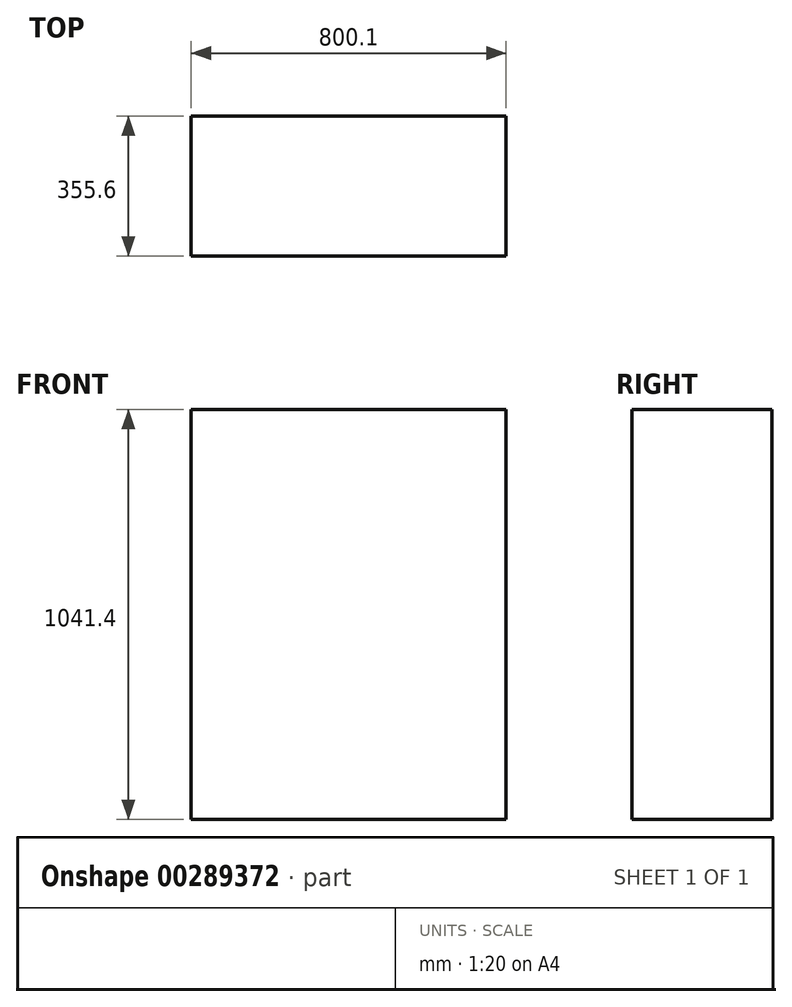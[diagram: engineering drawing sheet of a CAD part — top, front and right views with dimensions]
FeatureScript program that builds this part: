
annotation { "Feature Type Name" : "Feature", "Feature Type Description" : "" }
export const myFeature = defineFeature(function(context is Context, id is Id, definition is map)
    precondition{}
    {
        {
            var Q0;
            Q0=qCreatedBy(makeId("Front.planeOp"),FACE);
            var sketch = newSketch(context, id + "F0", { "sketchPlane" : qUnion([Q0])});
            skLineSegment(sketch, "E0.bottom", {"start": v(400.05, -520.7) * mm, "end": v(-400.05, -520.7) * mm});
            skLineSegment(sketch, "E0.top", {"start": v(400.05, 520.7) * mm, "end": v(-400.05, 520.7) * mm});
            skLineSegment(sketch, "E0.left", {"start": v(400.05, -520.7) * mm, "end": v(400.05, 520.7) * mm});
            skLineSegment(sketch, "E0.right", {"start": v(-400.05, -520.7) * mm, "end": v(-400.05, 520.7) * mm});
            skPoint(sketch, "E0.middle", {"position": v(0, 0) * mm});
            skSolve(sketch);
        }
        {
            var Q0;
            Q0=makeQuery(id+"F0.imprint","IMPRINT",FACE,{"disambiguationData":[TD([[makeQuery(id+"F0.imprint","IMPRINT",EDGE,{"derivedFrom":sQuery(id+"F0.wireOp",EDGE,"E0.bottom")}),-1.0]])]});
            extrude(context, id + "F1", {"entities" : qUnion([Q0]), "depth" : 355.6 * mm});
        }
    });
